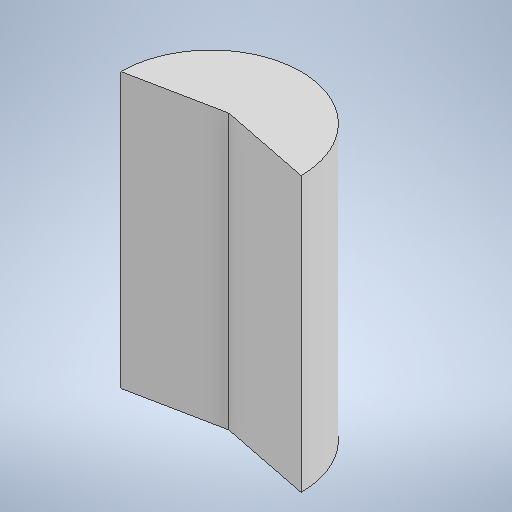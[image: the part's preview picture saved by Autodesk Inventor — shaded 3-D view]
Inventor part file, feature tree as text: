
AUTODESK INVENTOR PART (.ipt)
format: ipt  version: 2025.2 (Build 292293000, 293)  size: 199,680 bytes
history: native  units: in
note: dims shown in document units (in); Inventor stores cm internally (conversion verified against a paired STEP export)
features: extrude x1, sketch x1
ambient origin geometry x8: Origin, YZ Plane, XZ Plane, XY Plane, X Axis, Y Axis, Z Axis, Center Point
bodies: Solid1 (feature_tree)
feature tree (2):
  extrude  "Extrusion1"  Depth=0.1969in
  sketch  "Sketch1"  dims[d0=1.9685in d1=0.1969in d2=3.0in d3=0.0in]
